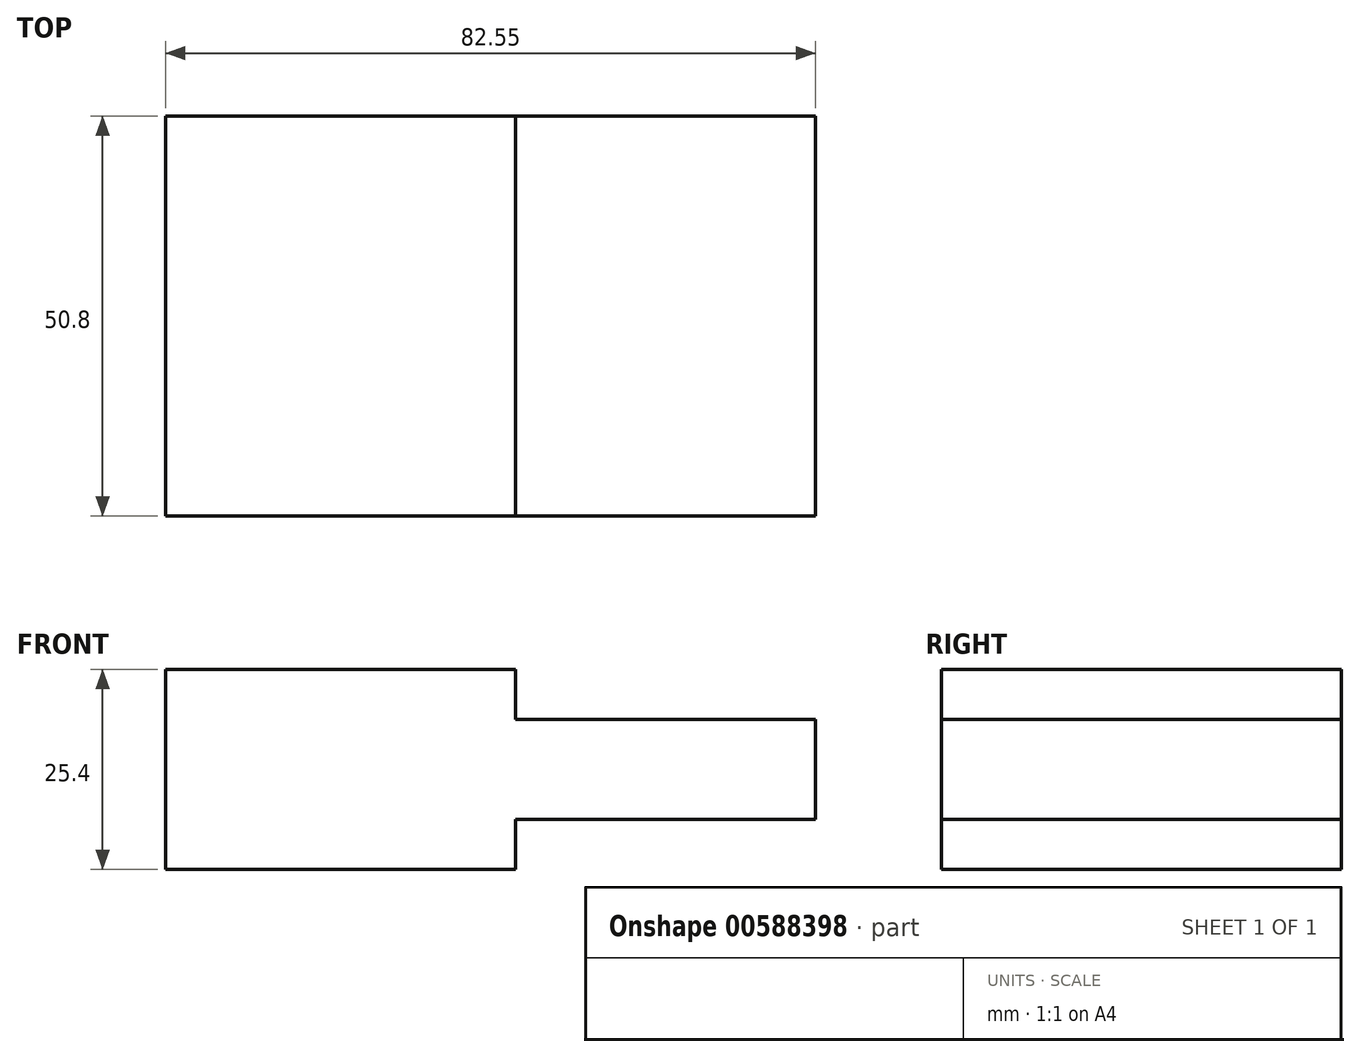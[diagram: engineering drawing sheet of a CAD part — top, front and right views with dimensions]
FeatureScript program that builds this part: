
annotation { "Feature Type Name" : "Feature", "Feature Type Description" : "" }
export const myFeature = defineFeature(function(context is Context, id is Id, definition is map)
    precondition{}
    {
        {
            var Q0;
            Q0=qCreatedBy(makeId("Front.planeOp"),FACE);
            var sketch = newSketch(context, id + "F0", { "sketchPlane" : qUnion([Q0])});
            skLineSegment(sketch, "E0", {"start": v(0, 0) * mm, "end": v(0, 25.4) * mm});
            skLineSegment(sketch, "E1", {"start": v(0, 25.4) * mm, "end": v(44.45, 25.4) * mm});
            skLineSegment(sketch, "E2", {"start": v(44.45, 25.4) * mm, "end": v(44.45, 19.05) * mm});
            skLineSegment(sketch, "E3", {"start": v(44.45, 19.05) * mm, "end": v(82.55, 19.05) * mm});
            skLineSegment(sketch, "E4", {"start": v(82.55, 19.05) * mm, "end": v(82.55, 6.35) * mm});
            skLineSegment(sketch, "E5", {"start": v(82.55, 6.35) * mm, "end": v(44.45, 6.35) * mm});
            skLineSegment(sketch, "E6", {"start": v(44.45, 6.35) * mm, "end": v(44.45, 0) * mm});
            skLineSegment(sketch, "E7", {"start": v(44.45, 0) * mm, "end": v(0, 0) * mm});
            skSolve(sketch);
        }
        {
            var Q0;
            Q0=makeQuery(id+"F0.imprint","IMPRINT",FACE,{"disambiguationData":[TD([[makeQuery(id+"F0.imprint","IMPRINT",EDGE,{"derivedFrom":sQuery(id+"F0.wireOp",EDGE,"E0")}),-1.0]])]});
            extrude(context, id + "F1", {"entities" : qUnion([Q0]), "depth" : 50.8 * mm, "offsetDistance" : 25.4 * mm});
        }
    });
